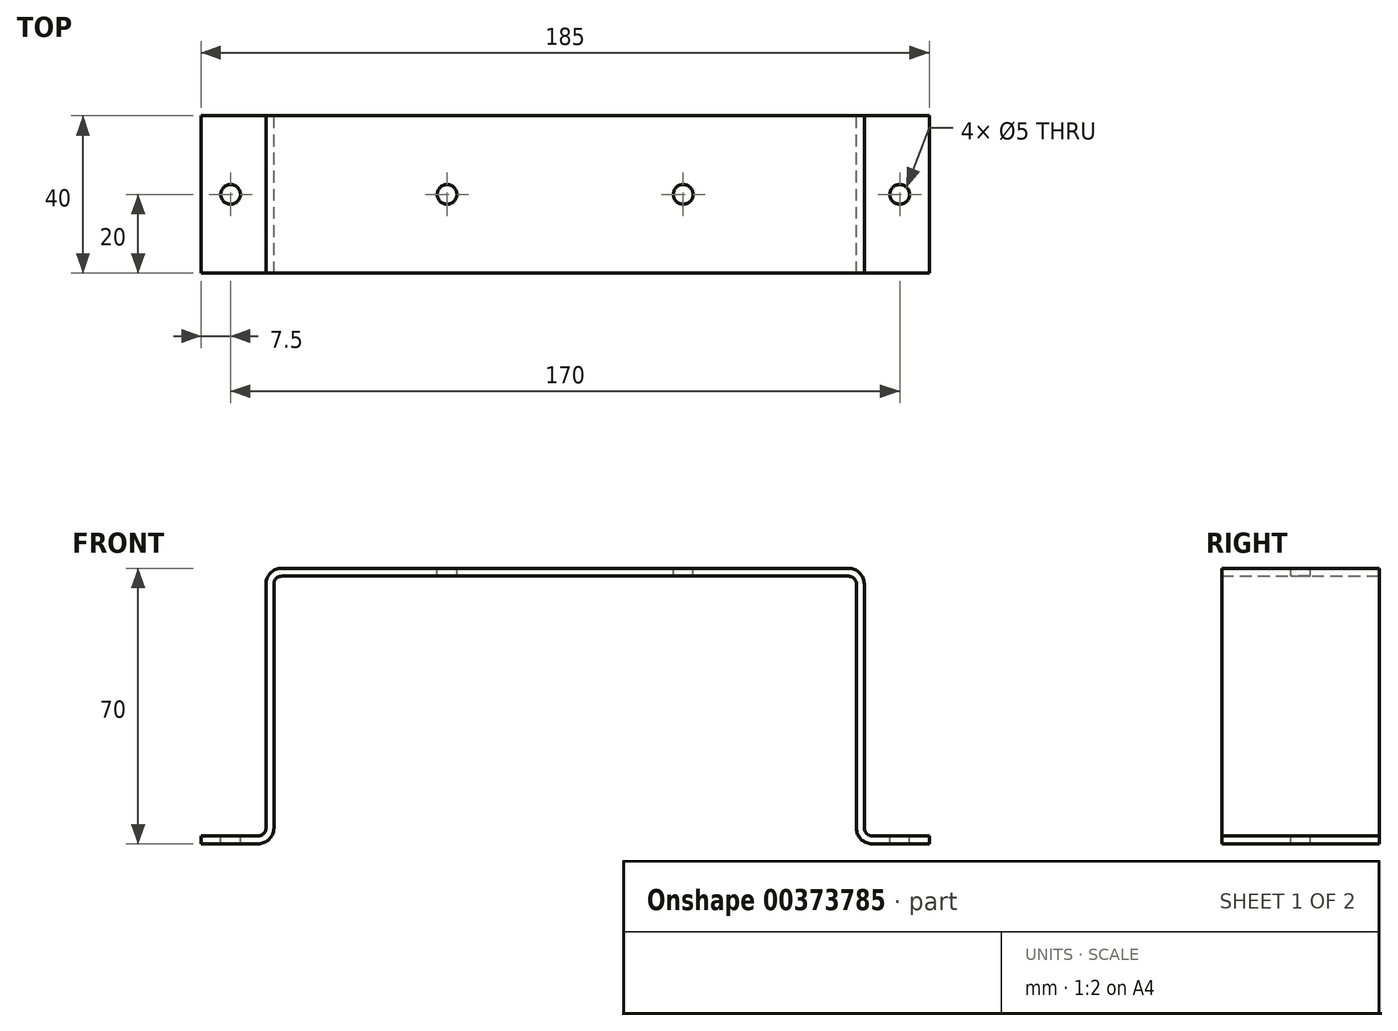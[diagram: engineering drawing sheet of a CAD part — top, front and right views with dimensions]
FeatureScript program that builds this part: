
annotation { "Feature Type Name" : "Feature", "Feature Type Description" : "" }
export const myFeature = defineFeature(function(context is Context, id is Id, definition is map)
    precondition{}
    {
        {
            var Q0;
            Q0=qCreatedBy(makeId("Front.planeOp"),FACE);
            var sketch = newSketch(context, id + "F0", { "sketchPlane" : qUnion([Q0])});
            skLineSegment(sketch, "E0", {"start": v(-92.5, 0) * mm, "end": v(-92.5, 2) * mm});
            skLineSegment(sketch, "E1", {"start": v(-92.5, 2) * mm, "end": v(-78, 2) * mm});
            skLineSegment(sketch, "E2", {"start": v(-76, 4) * mm, "end": v(-76, 66) * mm});
            skLineSegment(sketch, "E3", {"start": v(-72, 70) * mm, "end": v(0, 70) * mm});
            skLineSegment(sketch, "E4", {"start": v(0, 70) * mm, "end": v(0, 0) * mm, "construction": true});
            skLineSegment(sketch, "E5", {"start": v(-92.5, 0) * mm, "end": v(-78, 0) * mm});
            skLineSegment(sketch, "E6", {"start": v(-74, 4) * mm, "end": v(-74, 66) * mm});
            skLineSegment(sketch, "E7", {"start": v(-72, 68) * mm, "end": v(0, 68) * mm});
            skPoint(sketch, "E8.visualSharp", {"position": v(-76, 70) * mm});
            skArc(sketch, "E8.filletArc", {"start": v(-72, 70) * mm, "mid": v(-74.83, 68.83) * mm, "end": v(-76, 66) * mm});
            skPoint(sketch, "E9.visualSharp", {"position": v(-74, 0) * mm});
            skArc(sketch, "E9.filletArc", {"start": v(-78, 0) * mm, "mid": v(-75.17, 1.17) * mm, "end": v(-74, 4) * mm});
            skPoint(sketch, "E10.visualSharp", {"position": v(-74, 68) * mm});
            skArc(sketch, "E10.filletArc", {"start": v(-72, 68) * mm, "mid": v(-73.41, 67.41) * mm, "end": v(-74, 66) * mm});
            skPoint(sketch, "E11.visualSharp", {"position": v(-76, 2) * mm});
            skArc(sketch, "E11.filletArc", {"start": v(-78, 2) * mm, "mid": v(-76.59, 2.59) * mm, "end": v(-76, 4) * mm});
            skArc(sketch, "E12.MirrorCS", {"start": v(78, 2) * mm, "mid": v(76.59, 2.59) * mm, "end": v(76, 4) * mm});
            skArc(sketch, "E13.MirrorCS", {"start": v(72, 68) * mm, "mid": v(73.41, 67.41) * mm, "end": v(74, 66) * mm});
            skArc(sketch, "E14.MirrorCS", {"start": v(78, 0) * mm, "mid": v(75.17, 1.17) * mm, "end": v(74, 4) * mm});
            skLineSegment(sketch, "E15.MirrorCS", {"start": v(92.5, 0) * mm, "end": v(92.5, 2) * mm});
            skArc(sketch, "E16.MirrorCS", {"start": v(72, 70) * mm, "mid": v(74.83, 68.83) * mm, "end": v(76, 66) * mm});
            skPoint(sketch, "E17.MirrorP", {"position": v(76, 70) * mm});
            skPoint(sketch, "E18.MirrorP", {"position": v(74, 0) * mm});
            skPoint(sketch, "E19.MirrorP", {"position": v(74, 68) * mm});
            skPoint(sketch, "E20.MirrorP", {"position": v(76, 2) * mm});
            skLineSegment(sketch, "E21.MirrorCS", {"start": v(92.5, 2) * mm, "end": v(78, 2) * mm});
            skLineSegment(sketch, "E22.MirrorCS", {"start": v(76, 4) * mm, "end": v(76, 66) * mm});
            skLineSegment(sketch, "E23.MirrorCS", {"start": v(72, 68) * mm, "end": v(0, 68) * mm});
            skLineSegment(sketch, "E24.MirrorCS", {"start": v(74, 4) * mm, "end": v(74, 66) * mm});
            skLineSegment(sketch, "E25.MirrorCS", {"start": v(92.5, 0) * mm, "end": v(78, 0) * mm});
            skLineSegment(sketch, "E26.MirrorCS", {"start": v(72, 70) * mm, "end": v(0, 70) * mm});
            skSolve(sketch);
        }
        {
            var Q0;
            Q0=qSketchRegion(id+"F0",true);
            extrude(context, id + "F1", {"entities" : qUnion([Q0]), "endBound" : BoundingType.SYMMETRIC, "depth" : 40 * mm});
        }
        {
            var Q0;
            Q0=makeQuery(id+"F1.opExtrude","SWEPT_FACE",FACE,{"disambiguationData":[OSD([sQuery(id+"F0.wireOp",EDGE,"E1")])]});
            var sketch = newSketch(context, id + "F2", { "sketchPlane" : qUnion([Q0])});
            skCircle(sketch, "E27", {"center": v(-85, 0) * mm, "radius": 2.5 * mm});
            skPoint(sketch, "E27.centerSnap0", {"position": v(-92.5, 0) * mm});
            skCircle(sketch, "E28", {"center": v(85, 0) * mm, "radius": 2.5 * mm});
            skSolve(sketch);
        }
        {
            var Q0;
            Q0=qSketchRegion(id+"F2",true);
            extrude(context, id + "F3", {"entities" : qUnion([Q0]), "operationType" : NewBodyOperationType.REMOVE, "endBound" : BoundingType.THROUGH_ALL, "oppositeDirection" : true, "depth" : 25 * mm});
        }
        {
            var Q0;
            Q0=makeQuery(id+"F1.opExtrude","SWEPT_FACE",FACE,{"disambiguationData":[OSD([sQuery(id+"F0.wireOp",EDGE,"E3"),sQuery(id+"F0.wireOp",EDGE,"E26.MirrorCS")])]});
            var sketch = newSketch(context, id + "F4", { "sketchPlane" : qUnion([Q0])});
            skCircle(sketch, "E29", {"center": v(-30, 0) * mm, "radius": 2.5 * mm});
            skCircle(sketch, "E30", {"center": v(30, 0) * mm, "radius": 2.5 * mm});
            skSolve(sketch);
        }
        {
            var Q0;
            Q0=makeQuery(id+"F4.imprint","IMPRINT",FACE,{"disambiguationData":[TD([[makeQuery(id+"F4.imprint","IMPRINT",EDGE,{"derivedFrom":sQuery(id+"F4.wireOp",EDGE,"E29")}),1.0]])]});
            var Q1;
            Q1=makeQuery(id+"F4.imprint","IMPRINT",FACE,{"disambiguationData":[TD([[makeQuery(id+"F4.imprint","IMPRINT",EDGE,{"derivedFrom":sQuery(id+"F4.wireOp",EDGE,"E30")}),1.0]])]});
            extrude(context, id + "F5", {"entities" : qUnion([Q0, Q1]), "operationType" : NewBodyOperationType.REMOVE, "oppositeDirection" : true, "depth" : 25 * mm});
        }
    });
